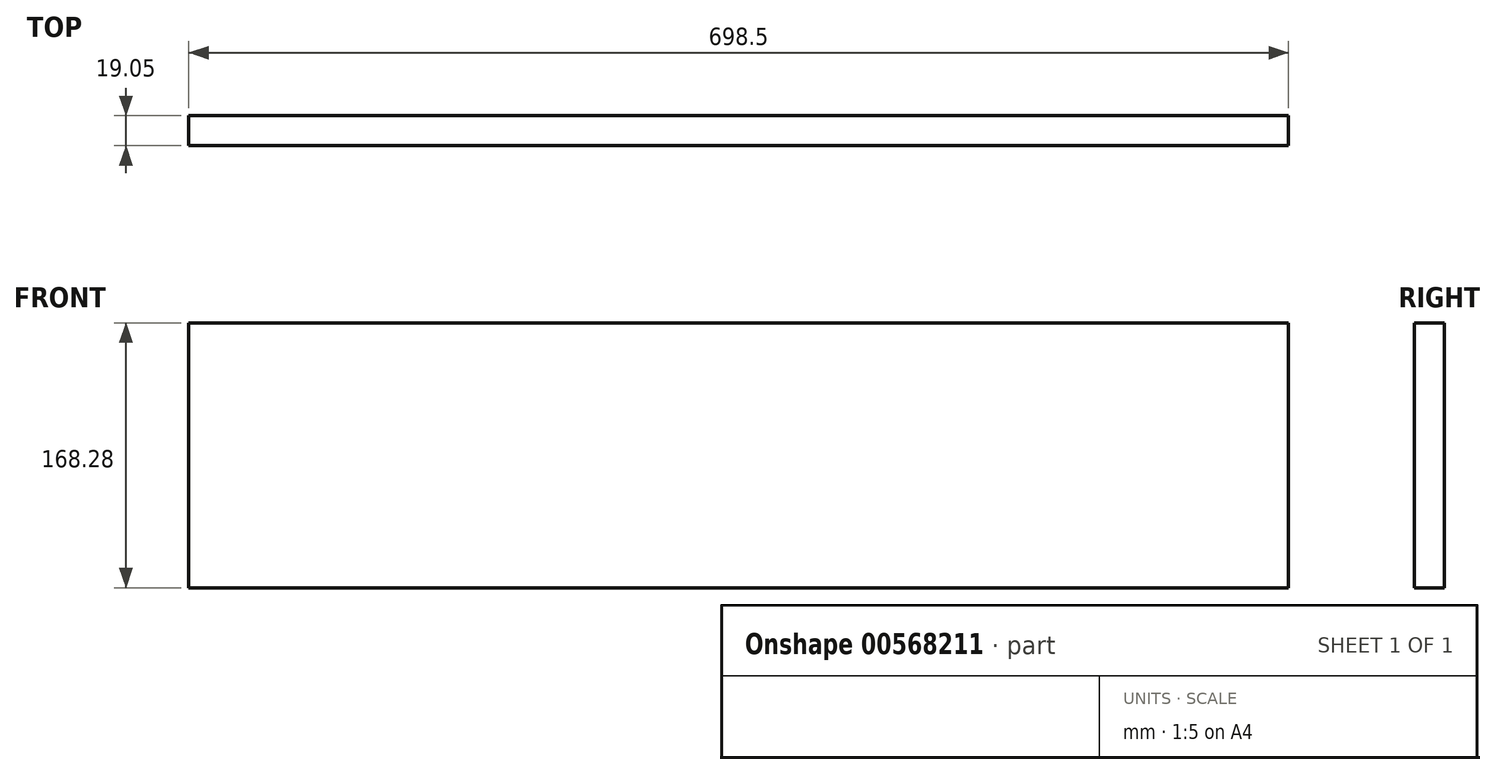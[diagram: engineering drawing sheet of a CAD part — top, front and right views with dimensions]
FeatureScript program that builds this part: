
annotation { "Feature Type Name" : "Feature", "Feature Type Description" : "" }
export const myFeature = defineFeature(function(context is Context, id is Id, definition is map)
    precondition{}
    {
        {
            var Q0;
            Q0=qCreatedBy(makeId("Front.planeOp"),FACE);
            var sketch = newSketch(context, id + "F0", { "sketchPlane" : qUnion([Q0])});
            skLineSegment(sketch, "E0.bottom", {"start": v(0, 0) * mm, "end": v(698.5, 0) * mm});
            skLineSegment(sketch, "E0.top", {"start": v(0, 168.28) * mm, "end": v(698.5, 168.28) * mm});
            skLineSegment(sketch, "E0.left", {"start": v(0, 0) * mm, "end": v(0, 168.28) * mm});
            skLineSegment(sketch, "E0.right", {"start": v(698.5, 0) * mm, "end": v(698.5, 168.28) * mm});
            skSolve(sketch);
        }
        {
            var Q0;
            Q0=makeQuery(id+"F0.imprint","IMPRINT",FACE,{"disambiguationData":[TD([[makeQuery(id+"F0.imprint","IMPRINT",EDGE,{"derivedFrom":sQuery(id+"F0.wireOp",EDGE,"E0.bottom")}),1.0]])]});
            extrude(context, id + "F1", {"entities" : qUnion([Q0]), "depth" : 19.05 * mm, "offsetDistance" : 25.4 * mm});
        }
    });
